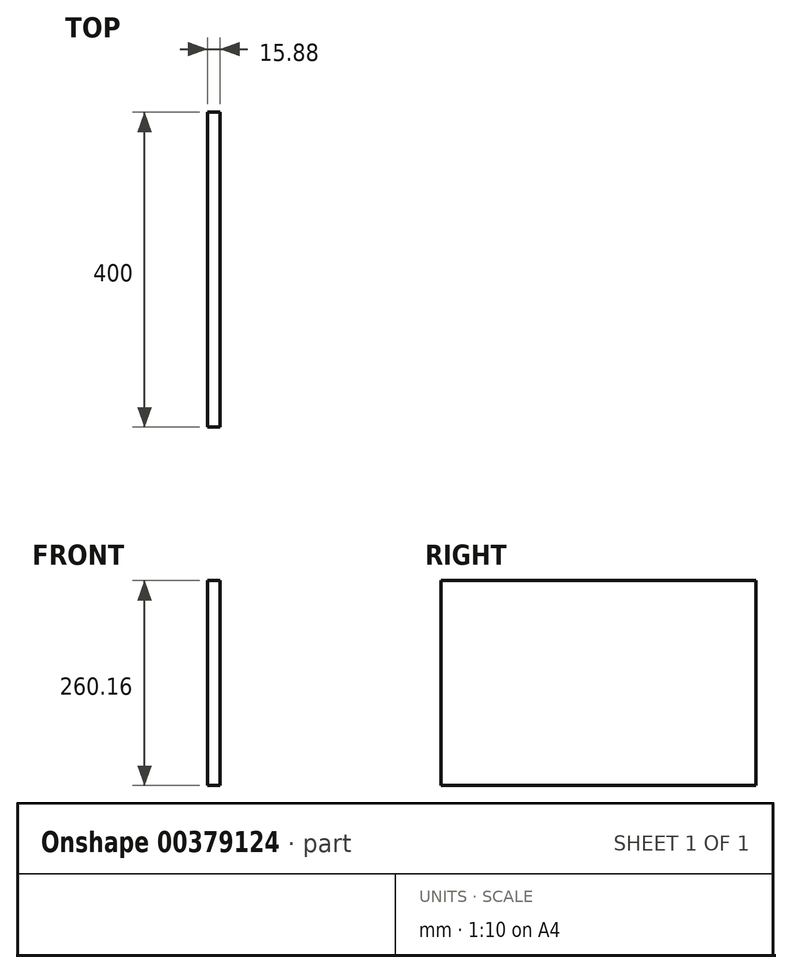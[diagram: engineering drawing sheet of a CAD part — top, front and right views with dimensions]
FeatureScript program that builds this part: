
annotation { "Feature Type Name" : "Feature", "Feature Type Description" : "" }
export const myFeature = defineFeature(function(context is Context, id is Id, definition is map)
    precondition{}
    {
        {
            var Q0;
            Q0=qCreatedBy(makeId("Front.planeOp"),FACE);
            var sketch = newSketch(context, id + "F0", { "sketchPlane" : qUnion([Q0])});
            skLineSegment(sketch, "E0.bottom", {"start": v(7.94, -130.08) * mm, "end": v(-7.94, -130.08) * mm});
            skLineSegment(sketch, "E0.top", {"start": v(7.94, 130.08) * mm, "end": v(-7.94, 130.08) * mm});
            skLineSegment(sketch, "E0.left", {"start": v(7.94, -130.08) * mm, "end": v(7.94, 130.08) * mm});
            skLineSegment(sketch, "E0.right", {"start": v(-7.94, -130.08) * mm, "end": v(-7.94, 130.08) * mm});
            skPoint(sketch, "E0.middle", {"position": v(0, 0) * mm});
            skSolve(sketch);
        }
        {
            var Q0;
            Q0=makeQuery(id+"F0.imprint","IMPRINT",FACE,{"disambiguationData":[TD([[makeQuery(id+"F0.imprint","IMPRINT",EDGE,{"derivedFrom":sQuery(id+"F0.wireOp",EDGE,"E0.bottom")}),-1.0]])]});
            extrude(context, id + "F1", {"entities" : qUnion([Q0]), "depth" : 400 * mm});
        }
    });
